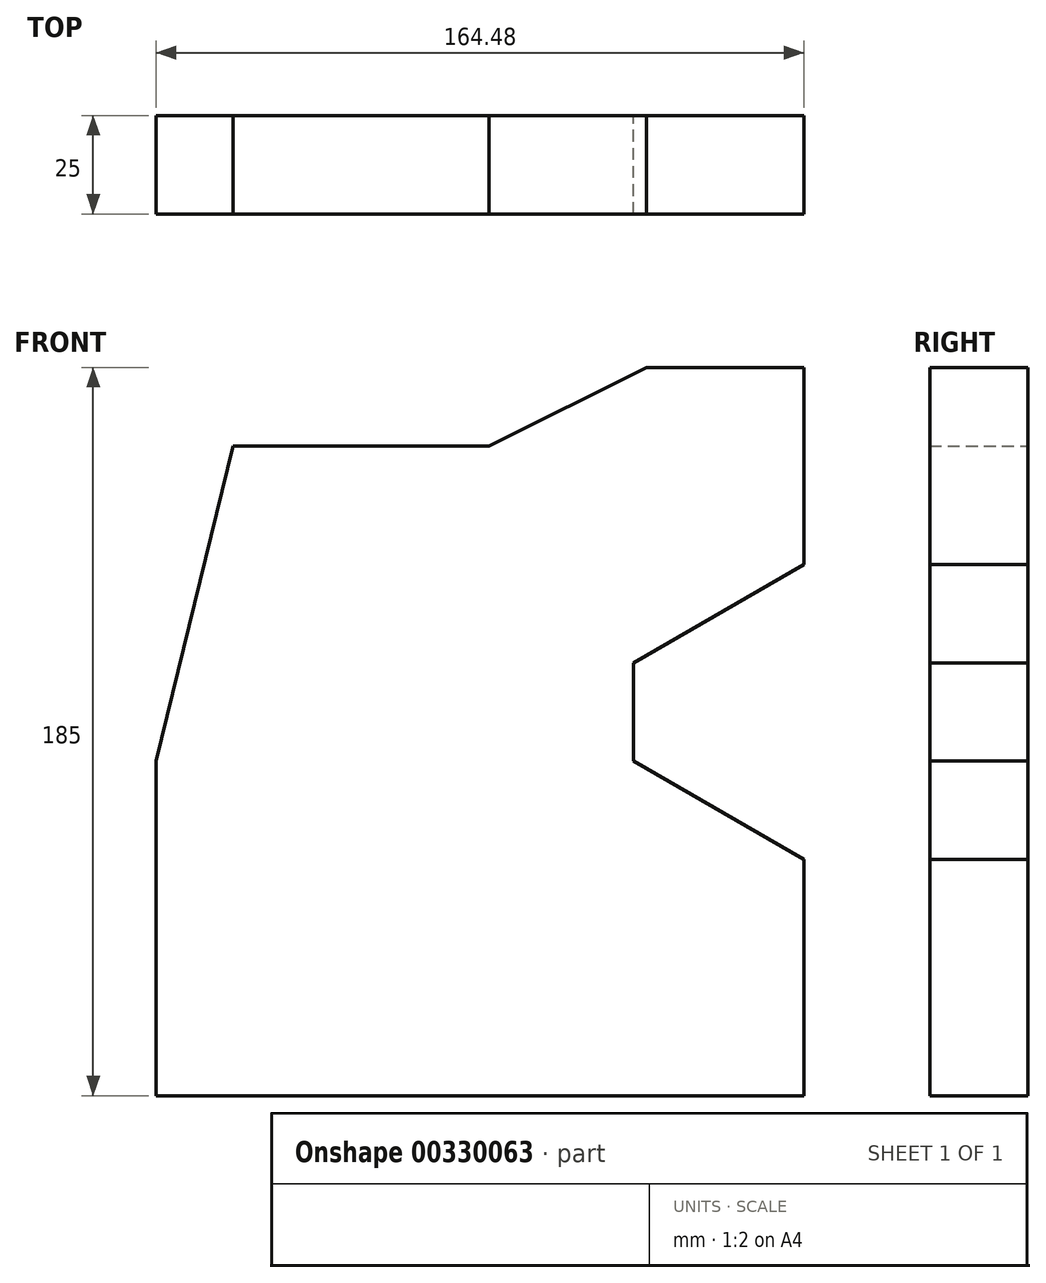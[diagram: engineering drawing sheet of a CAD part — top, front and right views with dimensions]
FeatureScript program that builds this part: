
annotation { "Feature Type Name" : "Feature", "Feature Type Description" : "" }
export const myFeature = defineFeature(function(context is Context, id is Id, definition is map)
    precondition{}
    {
        {
            var Q0;
            Q0=qCreatedBy(makeId("Front.planeOp"),FACE);
            var sketch = newSketch(context, id + "F0", { "sketchPlane" : qUnion([Q0])});
            skLineSegment(sketch, "E0", {"start": v(-141.38, 28.64) * mm, "end": v(-141.38, 3.64) * mm});
            skLineSegment(sketch, "E1", {"start": v(-141.38, 3.64) * mm, "end": v(-98.07, -21.36) * mm});
            skLineSegment(sketch, "E2", {"start": v(-141.38, 28.64) * mm, "end": v(-98.07, 53.64) * mm});
            skPoint(sketch, "E3.end.orphan", {"position": v(-75.13, 28.64) * mm});
            skPoint(sketch, "E4.end.orphan", {"position": v(-75.13, 3.64) * mm});
            skLineSegment(sketch, "E5", {"start": v(-98.07, -21.36) * mm, "end": v(-98.07, -81.36) * mm});
            skLineSegment(sketch, "E6", {"start": v(-98.07, -81.36) * mm, "end": v(-262.55, -81.36) * mm});
            skLineSegment(sketch, "E7", {"start": v(-141.38, 3.64) * mm, "end": v(-97.35, 3.64) * mm});
            skLineSegment(sketch, "E8", {"start": v(-262.55, -81.36) * mm, "end": v(-262.55, 3.64) * mm});
            skLineSegment(sketch, "E9", {"start": v(-98.07, 53.64) * mm, "end": v(-98.07, 103.64) * mm});
            skLineSegment(sketch, "E10", {"start": v(-98.07, 103.64) * mm, "end": v(-138.07, 103.64) * mm});
            skLineSegment(sketch, "E11", {"start": v(-138.07, 103.64) * mm, "end": v(-178.07, 83.64) * mm});
            skLineSegment(sketch, "E12", {"start": v(-178.07, 83.64) * mm, "end": v(-243.07, 83.64) * mm});
            skLineSegment(sketch, "E13", {"start": v(-243.07, 83.64) * mm, "end": v(-262.55, 3.64) * mm});
            skSolve(sketch);
        }
        {
            var Q0;
            Q0=makeQuery(id+"F0.imprint","IMPRINT",FACE,{"disambiguationData":[TD([[makeQuery(id+"F0.imprint","IMPRINT",EDGE,{"derivedFrom":sQuery(id+"F0.wireOp",EDGE,"E0")}),-1.0]])]});
            extrude(context, id + "F1", {"entities" : qUnion([Q0]), "depth" : 25 * mm});
        }
    });
